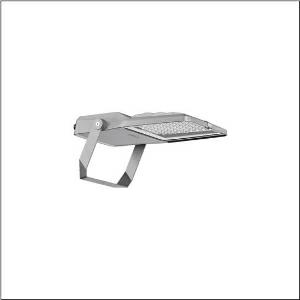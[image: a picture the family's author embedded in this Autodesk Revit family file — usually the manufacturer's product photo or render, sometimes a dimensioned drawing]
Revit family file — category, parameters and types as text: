
# Revit family: floodlight_fl_21_iq_mini___rs12_5xa7772d4b1a_8fae
name_source: partatom
category: Lighting Fixtures
units: mm (PartAtom-declared; Revit-internal decimal feet)

## family parameters
Cut with Voids When Loaded = No
Host = Face
Light Source = No
Part Type = Normal
Room Calculation Point = No
Round Connector Dimension = Use Diameter
Shared = No

## types (1)
- --- (1 x LED, 18810 lm, 143 W, 4000K)
    Apparent Load = 143 VA
    CIE Flux Codes = 79 92 99 100 100
    Color Rendering = 70
    Color Temperature = 4000K
    Default Elevation = 1800 mm
    Description = Floodlight FL 21 iQ mini, floodlight, primary light control with lens, of PMMA, primary optical cover: protective disc, of toughened safety glass, transparent, light distribution: RS12, light emission: direct distribution, installation type: surface-mounted, LED, High Power LED, rated luminous flux: 18.810lm, luminous efficacy: 132lm/W, light colour: 740, colour temperature: 4000K, control gear: iQ Street-Remote/DALI, control: Street-Remote, Auto-Match, Temp-Guard, Night-Set, Smart-Wire, Desk-Remote (wireless, voltage-free reading and setting of iQ features in the workshop via application-optimized NFC function/RFID function), optimised constant luminous flux control (CLO 2.0), with terminal, 6-pole, mains connection: 220..240V, AC, 50/60Hz, start of lifetime: 143W, end of service life: 152W, reduction: 61W, luminaire housing, of diecast aluminium, powder-coated, Siteco® metallic grey (DB 702S), corrosivity category C5 mid according to DIN EN ISO 12944, suitable for swimming pools, chlorine-resistant, sealing non-destructively replaceable, mounting bracket, of steel, galvanised, powder-coated, Siteco® metallic grey (DB 702S), protection rating (complete): IP66, insulation class (complete): insulation class II (safety insulation), certification: CE, ENEC, VDE, protection symbol: D, impact resistance: IK08, permissible operating ambient temperature: -40..+40°C, permissible operating ambient temperature for outdoor applications: -40..+50°C, standard: DIN EN 12944, LABS conformity tested according to VDMA 24364:2018-05, packaging unit: 1 piece

Light Distribution: RS12
    Height = 70 mm
    Lamp = 1 x LED
    Lamp Light Flux = 18810 lm
    Lamp Power = 143 W
    Lamp count = 1
    Length = 485 mm
    Luminous efficacy = 132 lm/W
    Manufacturer = Siteco
    ModVariant = No
    Model = 5XA7772D4B1A
    Number of Poles = 1
    OnlyDefault = Yes
    Power Factor = 1
    Product Name = Floodlight FL 21 iQ mini | RS12
    Product group = floodlight | pylon annexe
    ProductGroupID = 6200
    Protection Class = Protection class II
    Protection Degree = IP 66
    RLX_Detail_Level = 1
    RLX_Emergency_Light_Flux = 0 lm
    RLX_Emergency_Type = 0
    RLX_Emergency_Type_DB = No
    RlxData = <blob elided: 91273 chars, md5=d50616ba>
    Socket = socket
    Standby Power = 0 W
    System Light Flux = 18810 lm
    System Power = 143 W
    Type Comments = factory setting: luminous flux: 100 % | dim-lin: 254 | 730 mA
    Type Image = l_1006845.jpg
    URL = http://relux.com
    VarID = @adj_167300
    Voltage = 0 V
    Weight = 0.00 kg
    Width = 337 mm

## geometry (parser evidence)
native form markers: Blend x4, Sweep x13
no freeform markers — native parametric forms only
